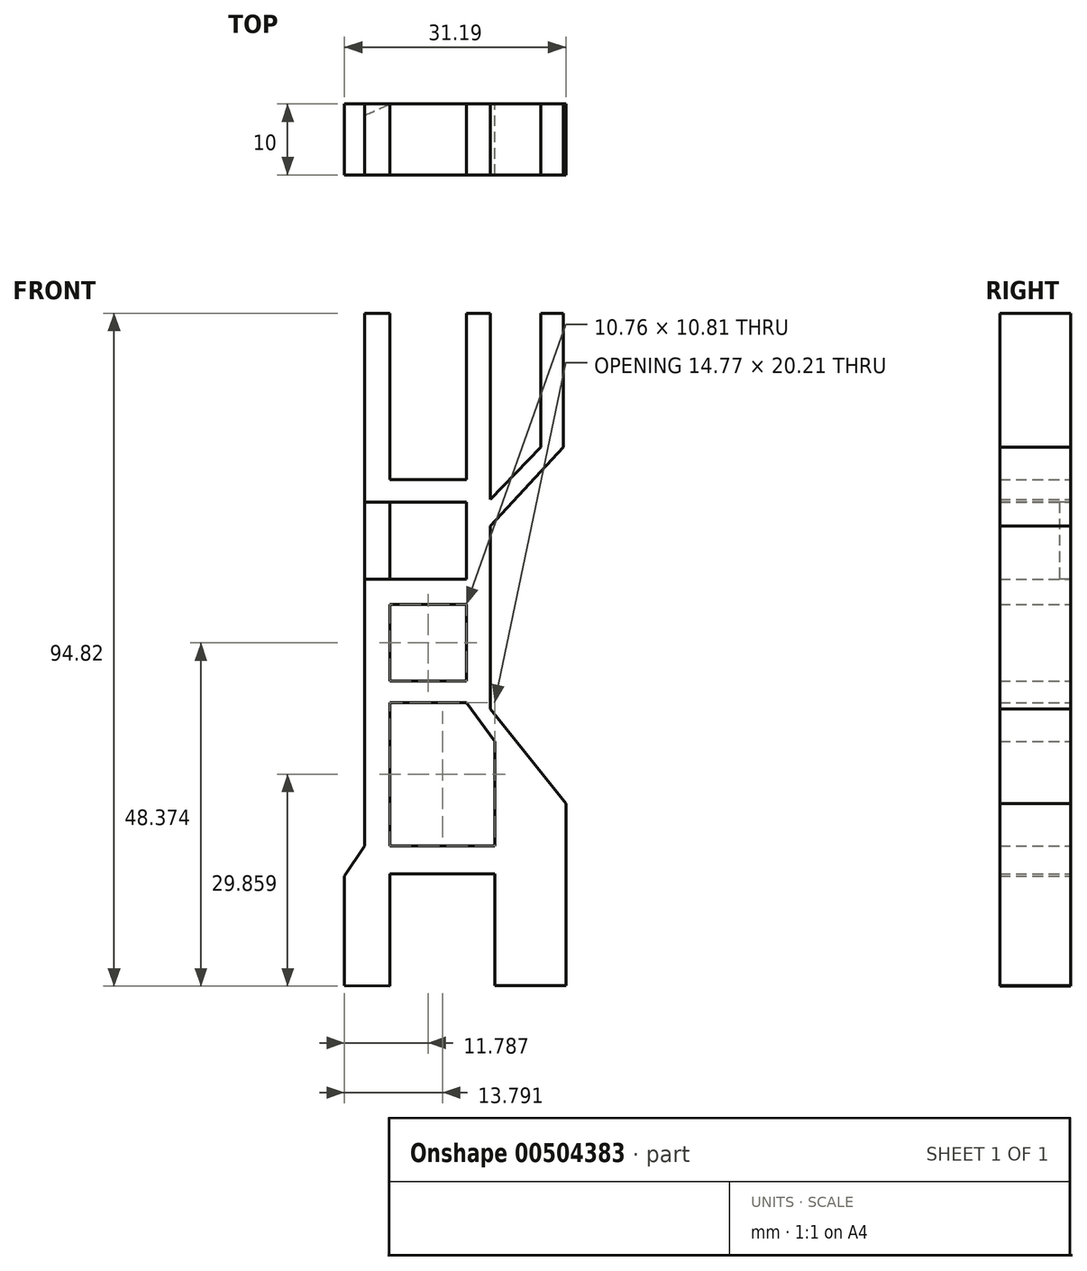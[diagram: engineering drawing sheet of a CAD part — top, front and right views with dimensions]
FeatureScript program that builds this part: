
annotation { "Feature Type Name" : "Feature", "Feature Type Description" : "" }
export const myFeature = defineFeature(function(context is Context, id is Id, definition is map)
    precondition{}
    {
        {
            var Q0;
            Q0=qCreatedBy(makeId("Front.planeOp"),FACE);
            var sketch = newSketch(context, id + "F0", { "sketchPlane" : qUnion([Q0])});
            skLineSegment(sketch, "E0", {"start": v(-57.68, 47.8) * mm, "end": v(-57.68, -27.27) * mm});
            skLineSegment(sketch, "E1", {"start": v(-57.68, -27.27) * mm, "end": v(-60.51, -31.51) * mm});
            skLineSegment(sketch, "E2", {"start": v(-60.51, -31.51) * mm, "end": v(-60.51, -46.95) * mm});
            skLineSegment(sketch, "E3", {"start": v(-57.68, 47.8) * mm, "end": v(-54.1, 47.8) * mm});
            skLineSegment(sketch, "E4", {"start": v(-54.1, 47.8) * mm, "end": v(-54.1, 24.36) * mm});
            skLineSegment(sketch, "E5", {"start": v(-54.1, 24.36) * mm, "end": v(-43.34, 24.36) * mm});
            skLineSegment(sketch, "E6", {"start": v(-43.34, 24.36) * mm, "end": v(-43.34, 47.8) * mm});
            skLineSegment(sketch, "E7", {"start": v(-43.34, 47.8) * mm, "end": v(-39.94, 47.8) * mm});
            skLineSegment(sketch, "E8", {"start": v(-39.94, 47.8) * mm, "end": v(-39.94, 21.57) * mm});
            skLineSegment(sketch, "E9", {"start": v(-43.34, 11.61) * mm, "end": v(-43.34, 10.32) * mm});
            skLineSegment(sketch, "E10.trimOffspring", {"start": v(-43.34, -1.28) * mm, "end": v(-43.34, -4.9) * mm});
            skPoint(sketch, "E11.start.orphan", {"position": v(-57.68, -32.3) * mm});
            skLineSegment(sketch, "E12", {"start": v(-54.1, -47.02) * mm, "end": v(-60.51, -46.95) * mm});
            skPoint(sketch, "E13.end.orphan", {"position": v(-54.1, 11.61) * mm});
            skPoint(sketch, "E14.end.orphan", {"position": v(-54.1, -1.28) * mm});
            skLineSegment(sketch, "E15", {"start": v(-43.34, 21.16) * mm, "end": v(-54.1, 21.16) * mm});
            skLineSegment(sketch, "E16", {"start": v(-43.34, 21.16) * mm, "end": v(-43.34, 10.32) * mm});
            skLineSegment(sketch, "E17", {"start": v(-43.34, 10.32) * mm, "end": v(-54.1, 10.32) * mm});
            skLineSegment(sketch, "E18", {"start": v(-43.34, 6.76) * mm, "end": v(-54.1, 6.76) * mm});
            skLineSegment(sketch, "E19", {"start": v(-54.1, 6.76) * mm, "end": v(-54.1, -4.05) * mm});
            skLineSegment(sketch, "E20", {"start": v(-54.1, -4.05) * mm, "end": v(-43.34, -4.05) * mm});
            skPoint(sketch, "E20.endSnap0", {"position": v(-43.34, -4.9) * mm});
            skLineSegment(sketch, "E21", {"start": v(-43.34, -7.06) * mm, "end": v(-54.1, -7.06) * mm});
            skLineSegment(sketch, "E22", {"start": v(-39.33, -12.52) * mm, "end": v(-39.33, -27.27) * mm});
            skPoint(sketch, "E23.end.orphan", {"position": v(-39.94, -27.27) * mm});
            skLineSegment(sketch, "E24", {"start": v(-39.33, -27.27) * mm, "end": v(-54.1, -27.27) * mm});
            skPoint(sketch, "E25.start.orphan", {"position": v(-43.34, -8.5) * mm});
            skLineSegment(sketch, "E26", {"start": v(-39.33, -12.52) * mm, "end": v(-43.34, -7.06) * mm});
            skLineSegment(sketch, "E27", {"start": v(-39.33, -31.19) * mm, "end": v(-39.33, -46.94) * mm});
            skLineSegment(sketch, "E28", {"start": v(-39.33, -46.94) * mm, "end": v(-29.32, -46.94) * mm});
            skLineSegment(sketch, "E29", {"start": v(-29.32, -46.94) * mm, "end": v(-29.32, -21.3) * mm});
            skLineSegment(sketch, "E30", {"start": v(-29.32, -21.3) * mm, "end": v(-39.94, -7.93) * mm});
            skLineSegment(sketch, "E31", {"start": v(-54.1, -31.19) * mm, "end": v(-54.1, -47.02) * mm});
            skLineSegment(sketch, "E32", {"start": v(-39.94, 17.8) * mm, "end": v(-29.67, 28.9) * mm});
            skLineSegment(sketch, "E33", {"start": v(-29.67, 28.9) * mm, "end": v(-29.67, 47.8) * mm});
            skLineSegment(sketch, "E34", {"start": v(-29.67, 47.8) * mm, "end": v(-32.86, 47.8) * mm});
            skLineSegment(sketch, "E35", {"start": v(-32.86, 47.8) * mm, "end": v(-32.86, 28.9) * mm});
            skLineSegment(sketch, "E36", {"start": v(-32.86, 28.9) * mm, "end": v(-39.94, 21.57) * mm});
            skLineSegment(sketch, "E37", {"start": v(-39.33, -31.19) * mm, "end": v(-54.1, -31.19) * mm});
            skLineSegment(sketch, "E38.trimOffspring", {"start": v(-39.94, 17.8) * mm, "end": v(-39.94, -7.93) * mm});
            skLineSegment(sketch, "E39.trimOffspring", {"start": v(-54.1, 21.16) * mm, "end": v(-54.1, 10.32) * mm});
            skLineSegment(sketch, "E40.trimOffspring", {"start": v(-43.34, 6.76) * mm, "end": v(-43.34, -1.28) * mm});
            skLineSegment(sketch, "E41.trimOffspring", {"start": v(-54.1, -7.06) * mm, "end": v(-54.1, -27.27) * mm});
            skSolve(sketch);
        }
        {
            var Q0;
            Q0=makeQuery(id+"F0.imprint","IMPRINT",FACE,{"disambiguationData":[TD([[makeQuery(id+"F0.imprint","IMPRINT",EDGE,{"derivedFrom":sQuery(id+"F0.wireOp",EDGE,"E0")}),1.0]])]});
            extrude(context, id + "F1", {"entities" : qUnion([Q0]), "depth" : 10 * mm, "offsetDistance" : 25 * mm});
        }
        {
            var Q0;
            Q0=makeQuery(id+"F1.opExtrude","CAP_EDGE",EDGE,{"disambiguationData":[OSD([sQuery(id+"F0.wireOp",EDGE,"E39.trimOffspring")])],"isStart":false});
            fillet(context, id + "F2", {"entities" : qUnion([Q0]), "radius" : 105.5 * mm, "tangentPropagation" : true, "allowEdgeOverflow" : false});
        }
    });
